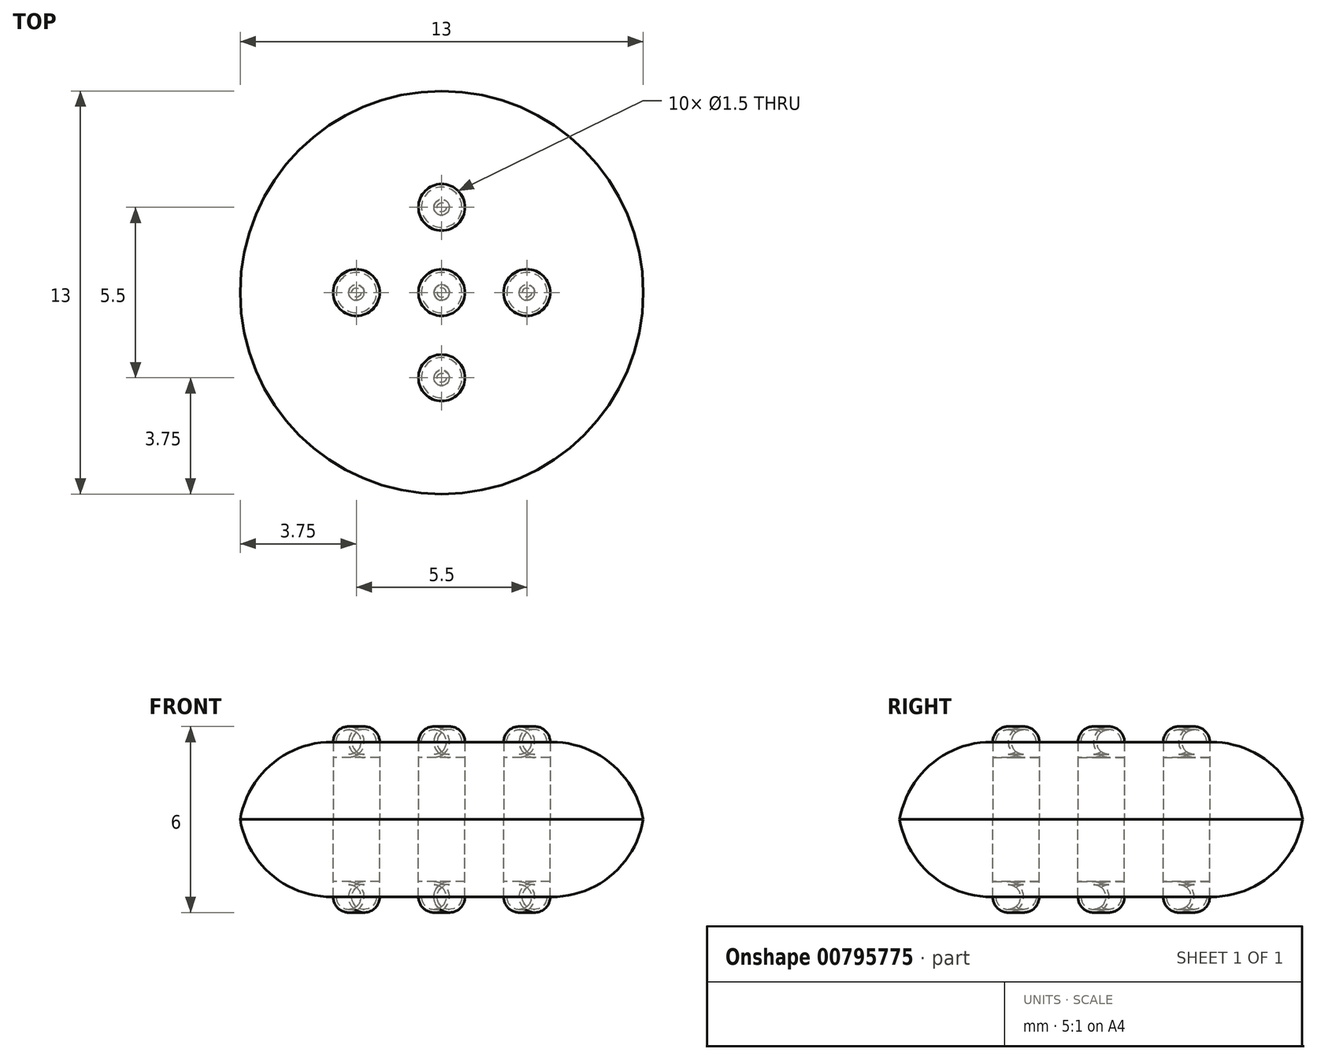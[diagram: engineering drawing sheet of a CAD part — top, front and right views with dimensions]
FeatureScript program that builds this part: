
annotation { "Feature Type Name" : "Feature", "Feature Type Description" : "" }
export const myFeature = defineFeature(function(context is Context, id is Id, definition is map)
    precondition{}
    {
        {
            var Q0;
            Q0=qCreatedBy(makeId("Top.planeOp"),FACE);
            var sketch = newSketch(context, id + "F0", { "sketchPlane" : qUnion([Q0])});
            skCircle(sketch, "E0", {"center": v(0, 0) * mm, "radius": 6.5 * mm});
            skCircle(sketch, "E1", {"center": v(0, 0) * mm, "radius": 2.75 * mm});
            skCircle(sketch, "E2", {"center": v(0, 0) * mm, "radius": 0.75 * mm});
            skCircle(sketch, "E3", {"center": v(0, 2.75) * mm, "radius": 0.75 * mm});
            skCircle(sketch, "E4", {"center": v(2.75, 0) * mm, "radius": 0.75 * mm});
            skCircle(sketch, "E5", {"center": v(0, -2.75) * mm, "radius": 0.75 * mm});
            skCircle(sketch, "E6", {"center": v(-2.75, 0) * mm, "radius": 0.75 * mm});
            skSolve(sketch);
        }
        {
            var Q0;
            Q0 = qSketchRegion(id + "F0", true);
            var Q1;
            Q1=makeQuery(id+"F0.imprint","IMPRINT",FACE,{"disambiguationData":[TD([[makeQuery(id+"F0.imprint","IMPRINT",EDGE,{"derivedFrom":sQuery(id+"F0.wireOp",EDGE,"E2")}),-1.0]])]});
            extrude(context, id + "F1", {"entities" : qUnion([Q0, Q1]), "depth" : 2.5 * mm, "offsetDistance" : 25 * mm});
        }
        {
            var Q0;
            Q0=makeQuery(id+"F1.opExtrude","CAP_EDGE",EDGE,{"disambiguationData":[OSD([sQuery(id+"F0.wireOp",EDGE,"E0")])],"isStart":false});
            fillet(context, id + "F2", {"entities" : qUnion([Q0]), "radius" : 3 * mm, "tangentPropagation" : true, "allowEdgeOverflow" : false});
        }
        {
            var Q0;
            {var subQ0=sQuery(id+"F0.wireOp",EDGE,"E6");var subQ1=sQuery(id+"F0.wireOp",EDGE,"E1");var subQ2=makeQuery(id+"F0.imprint","INTERSECT",VERTEX,{"disambiguationData":[OD(0.0)],"derivedFrom":[subQ1,subQ0]});Q0=makeQuery(id+"F0.imprint","IMPRINT",FACE,{"disambiguationData":[TD([[makeQuery(id+"F0.imprint","IMPRINT",EDGE,{"disambiguationData":[TD([[subQ2,-1.0]])],"derivedFrom":subQ1}),1.0]])]});}
            var Q1;
            {var subQ0=sQuery(id+"F0.wireOp",EDGE,"E6");var subQ1=sQuery(id+"F0.wireOp",EDGE,"E1");var subQ2=makeQuery(id+"F0.imprint","INTERSECT",VERTEX,{"disambiguationData":[OD(0.0)],"derivedFrom":[subQ1,subQ0]});Q1=makeQuery(id+"F0.imprint","IMPRINT",FACE,{"disambiguationData":[TD([[makeQuery(id+"F0.imprint","IMPRINT",EDGE,{"disambiguationData":[TD([[subQ2,-1.0]])],"derivedFrom":subQ1}),-1.0]])]});}
            var Q2;
            Q2=makeQuery(id+"F0.imprint","IMPRINT",FACE,{"disambiguationData":[TD([[makeQuery(id+"F0.imprint","IMPRINT",EDGE,{"derivedFrom":sQuery(id+"F0.wireOp",EDGE,"E2")}),1.0]])]});
            var Q3;
            {var subQ0=sQuery(id+"F0.wireOp",EDGE,"E3");var subQ1=sQuery(id+"F0.wireOp",EDGE,"E1");var subQ2=makeQuery(id+"F0.imprint","INTERSECT",VERTEX,{"disambiguationData":[OD(0.0)],"derivedFrom":[subQ1,subQ0]});Q3=makeQuery(id+"F0.imprint","IMPRINT",FACE,{"disambiguationData":[TD([[makeQuery(id+"F0.imprint","IMPRINT",EDGE,{"disambiguationData":[TD([[subQ2,-1.0]])],"derivedFrom":subQ1}),-1.0]])]});}
            var Q4;
            {var subQ0=sQuery(id+"F0.wireOp",EDGE,"E3");var subQ1=sQuery(id+"F0.wireOp",EDGE,"E1");var subQ2=makeQuery(id+"F0.imprint","INTERSECT",VERTEX,{"disambiguationData":[OD(0.0)],"derivedFrom":[subQ1,subQ0]});Q4=makeQuery(id+"F0.imprint","IMPRINT",FACE,{"disambiguationData":[TD([[makeQuery(id+"F0.imprint","IMPRINT",EDGE,{"disambiguationData":[TD([[subQ2,-1.0]])],"derivedFrom":subQ1}),1.0]])]});}
            var Q5;
            {var subQ0=sQuery(id+"F0.wireOp",EDGE,"E4");var subQ1=sQuery(id+"F0.wireOp",EDGE,"E1");var subQ2=makeQuery(id+"F0.imprint","INTERSECT",VERTEX,{"disambiguationData":[OD(0.0)],"derivedFrom":[subQ1,subQ0]});Q5=makeQuery(id+"F0.imprint","IMPRINT",FACE,{"disambiguationData":[TD([[makeQuery(id+"F0.imprint","IMPRINT",EDGE,{"disambiguationData":[TD([[subQ2,1.0]])],"derivedFrom":subQ1}),1.0]])]});}
            var Q6;
            {var subQ0=sQuery(id+"F0.wireOp",EDGE,"E4");var subQ1=sQuery(id+"F0.wireOp",EDGE,"E1");var subQ2=makeQuery(id+"F0.imprint","INTERSECT",VERTEX,{"disambiguationData":[OD(0.0)],"derivedFrom":[subQ1,subQ0]});Q6=makeQuery(id+"F0.imprint","IMPRINT",FACE,{"disambiguationData":[TD([[makeQuery(id+"F0.imprint","IMPRINT",EDGE,{"disambiguationData":[TD([[subQ2,1.0]])],"derivedFrom":subQ1}),-1.0]])]});}
            var Q7;
            {var subQ0=sQuery(id+"F0.wireOp",EDGE,"E5");var subQ1=sQuery(id+"F0.wireOp",EDGE,"E1");var subQ2=makeQuery(id+"F0.imprint","INTERSECT",VERTEX,{"disambiguationData":[OD(0.0)],"derivedFrom":[subQ1,subQ0]});Q7=makeQuery(id+"F0.imprint","IMPRINT",FACE,{"disambiguationData":[TD([[makeQuery(id+"F0.imprint","IMPRINT",EDGE,{"disambiguationData":[TD([[subQ2,-1.0]])],"derivedFrom":subQ1}),1.0]])]});}
            var Q8;
            {var subQ0=sQuery(id+"F0.wireOp",EDGE,"E5");var subQ1=sQuery(id+"F0.wireOp",EDGE,"E1");var subQ2=makeQuery(id+"F0.imprint","INTERSECT",VERTEX,{"disambiguationData":[OD(0.0)],"derivedFrom":[subQ1,subQ0]});Q8=makeQuery(id+"F0.imprint","IMPRINT",FACE,{"disambiguationData":[TD([[makeQuery(id+"F0.imprint","IMPRINT",EDGE,{"disambiguationData":[TD([[subQ2,-1.0]])],"derivedFrom":subQ1}),-1.0]])]});}
            extrude(context, id + "F3", {"entities" : qUnion([Q0, Q1, Q2, Q3, Q4, Q5, Q6, Q7, Q8]), "depth" : 2 * mm, "offsetDistance" : 25 * mm});
        }
        {
            var Q0;
            Q0=makeQuery(id+"F3.opExtrude","CAP_FACE",FACE,{"disambiguationData":[OSD([sQuery(id+"F0.wireOp",EDGE,"E6")])],"isStart":false});
            var Q1;
            Q1=makeQuery(id+"F3.opExtrude","CAP_FACE",FACE,{"disambiguationData":[OSD([sQuery(id+"F0.wireOp",EDGE,"E2")])],"isStart":false});
            var Q2;
            Q2=makeQuery(id+"F3.opExtrude","CAP_FACE",FACE,{"disambiguationData":[OSD([sQuery(id+"F0.wireOp",EDGE,"E3")])],"isStart":false});
            var Q3;
            Q3=makeQuery(id+"F3.opExtrude","CAP_FACE",FACE,{"disambiguationData":[OSD([sQuery(id+"F0.wireOp",EDGE,"E4")])],"isStart":false});
            var Q4;
            Q4=makeQuery(id+"F3.opExtrude","CAP_FACE",FACE,{"disambiguationData":[OSD([sQuery(id+"F0.wireOp",EDGE,"E5")])],"isStart":false});
            extrude(context, id + "F4", {"entities" : qUnion([Q0, Q1, Q2, Q3, Q4]), "depth" : 0.5 * mm, "offsetDistance" : 25 * mm});
        }
        {
            var Q0;
            Q0=makeQuery(id+"F4.opExtrude","CAP_EDGE",EDGE,{"disambiguationData":[OSD([sQuery(id+"F0.wireOp",EDGE,"E4")])],"isStart":true});
            var Q1;
            Q1=makeQuery(id+"F4.opExtrude","CAP_EDGE",EDGE,{"disambiguationData":[OSD([sQuery(id+"F0.wireOp",EDGE,"E5")])],"isStart":true});
            var Q2;
            Q2=makeQuery(id+"F4.opExtrude","CAP_EDGE",EDGE,{"disambiguationData":[OSD([sQuery(id+"F0.wireOp",EDGE,"E2")])],"isStart":true});
            var Q3;
            Q3=makeQuery(id+"F4.opExtrude","CAP_EDGE",EDGE,{"disambiguationData":[OSD([sQuery(id+"F0.wireOp",EDGE,"E3")])],"isStart":true});
            var Q4;
            Q4=makeQuery(id+"F4.opExtrude","CAP_EDGE",EDGE,{"disambiguationData":[OSD([sQuery(id+"F0.wireOp",EDGE,"E6")])],"isStart":true});
            fillet(context, id + "F5", {"entities" : qUnion([Q0, Q1, Q2, Q3, Q4]), "radius" : 0.5 * mm, "tangentPropagation" : true, "allowEdgeOverflow" : false});
        }
        {
            var Q0;
            Q0=makeQuery(id+"F4.opExtrude","CAP_FACE",FACE,{"disambiguationData":[OSD([sQuery(id+"F0.wireOp",EDGE,"E4")])],"isStart":false});
            var Q1;
            Q1=makeQuery(id+"F4.opExtrude","CAP_FACE",FACE,{"disambiguationData":[OSD([sQuery(id+"F0.wireOp",EDGE,"E5")])],"isStart":false});
            var Q2;
            Q2=makeQuery(id+"F4.opExtrude","CAP_FACE",FACE,{"disambiguationData":[OSD([sQuery(id+"F0.wireOp",EDGE,"E2")])],"isStart":false});
            var Q3;
            Q3=makeQuery(id+"F4.opExtrude","CAP_FACE",FACE,{"disambiguationData":[OSD([sQuery(id+"F0.wireOp",EDGE,"E3")])],"isStart":false});
            var Q4;
            Q4=makeQuery(id+"F4.opExtrude","CAP_FACE",FACE,{"disambiguationData":[OSD([sQuery(id+"F0.wireOp",EDGE,"E6")])],"isStart":false});
            shell(context, id + "F6", {"entities" : qUnion([Q0, Q1, Q2, Q3, Q4]), "thickness" : 0.1 * mm});
        }
        {
            var Q0;
            Q0=makeQuery(id+"F3.opExtrude","SWEPT_BODY",BODY,{"disambiguationData":[OSD([sQuery(id+"F0.wireOp",EDGE,"E4")])]});
            var Q1;
            Q1=makeQuery(id+"F3.opExtrude","SWEPT_BODY",BODY,{"disambiguationData":[OSD([sQuery(id+"F0.wireOp",EDGE,"E5")])]});
            var Q2;
            Q2=makeQuery(id+"F3.opExtrude","SWEPT_BODY",BODY,{"disambiguationData":[OSD([sQuery(id+"F0.wireOp",EDGE,"E6")])]});
            var Q3;
            Q3=makeQuery(id+"F3.opExtrude","SWEPT_BODY",BODY,{"disambiguationData":[OSD([sQuery(id+"F0.wireOp",EDGE,"E2")])]});
            var Q4;
            Q4=makeQuery(id+"F3.opExtrude","SWEPT_BODY",BODY,{"disambiguationData":[OSD([sQuery(id+"F0.wireOp",EDGE,"E3")])]});
            var Q5;
            Q5=makeQuery(id+"F1.opExtrude","SWEPT_BODY",BODY,{"disambiguationData":[OSD([sQuery(id+"F0.wireOp",EDGE,"E0"),sQuery(id+"F0.wireOp",EDGE,"E2"),sQuery(id+"F0.wireOp",EDGE,"E3"),sQuery(id+"F0.wireOp",EDGE,"E4"),sQuery(id+"F0.wireOp",EDGE,"E5"),sQuery(id+"F0.wireOp",EDGE,"E6")])]});
            var Q6;
            Q6=makeQuery(id+"F4.opExtrude","SWEPT_BODY",BODY,{"disambiguationData":[OSD([sQuery(id+"F0.wireOp",EDGE,"E4")])]});
            var Q7;
            Q7=makeQuery(id+"F4.opExtrude","SWEPT_BODY",BODY,{"disambiguationData":[OSD([sQuery(id+"F0.wireOp",EDGE,"E2")])]});
            var Q8;
            Q8=makeQuery(id+"F4.opExtrude","SWEPT_BODY",BODY,{"disambiguationData":[OSD([sQuery(id+"F0.wireOp",EDGE,"E3")])]});
            var Q9;
            Q9=makeQuery(id+"F4.opExtrude","SWEPT_BODY",BODY,{"disambiguationData":[OSD([sQuery(id+"F0.wireOp",EDGE,"E6")])]});
            var Q10;
            Q10=makeQuery(id+"F4.opExtrude","SWEPT_BODY",BODY,{"disambiguationData":[OSD([sQuery(id+"F0.wireOp",EDGE,"E5")])]});
            var Q11;
            Q11=qCreatedBy(makeId("Top.planeOp"),FACE);
            mirror(context, id + "F7", {"entities" : qUnion([Q0, Q1, Q2, Q3, Q4, Q5, Q6, Q7, Q8, Q9, Q10]), "mirrorPlane" : qUnion([Q11])});
        }
    });
